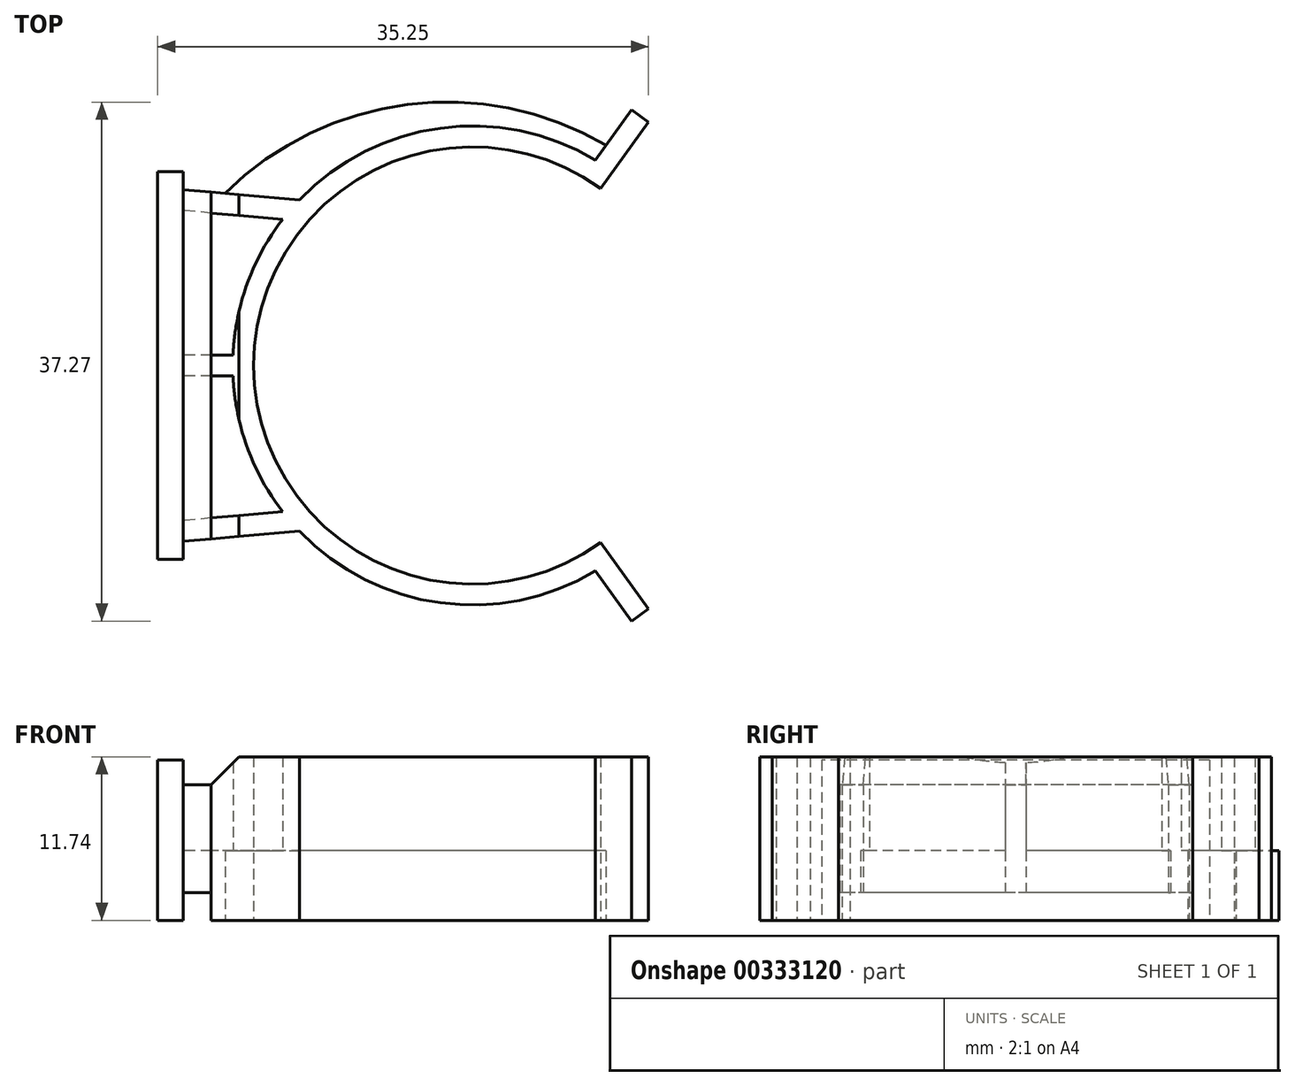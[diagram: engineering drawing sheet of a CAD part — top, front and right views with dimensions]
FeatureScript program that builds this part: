
annotation { "Feature Type Name" : "Feature", "Feature Type Description" : "" }
export const myFeature = defineFeature(function(context is Context, id is Id, definition is map)
    precondition{}
    {
        {
            var Q0;
            Q0=qCreatedBy(makeId("Top.planeOp"),FACE);
            var sketch = newSketch(context, id + "F0", { "sketchPlane" : qUnion([Q0])});
            skLineSegment(sketch, "E0.bottom", {"start": v(0, 13.91) * mm, "end": v(1.84, 13.91) * mm});
            skLineSegment(sketch, "E0.top", {"start": v(0, -13.91) * mm, "end": v(1.84, -13.91) * mm});
            skLineSegment(sketch, "E0.left", {"start": v(0, 13.91) * mm, "end": v(0, -13.91) * mm});
            skLineSegment(sketch, "E0.right", {"start": v(1.84, 13.91) * mm, "end": v(1.84, -13.91) * mm});
            skPoint(sketch, "E1", {"position": v(0, 0) * mm});
            skCircle(sketch, "E2", {"center": v(22.6, 0) * mm, "radius": 15.7 * mm});
            skLineSegment(sketch, "E3", {"start": v(31.8, 12.72) * mm, "end": v(31.8, -12.72) * mm, "construction": true});
            skLineSegment(sketch, "E4", {"start": v(1.84, 12.63) * mm, "end": v(1.84, -12.63) * mm, "construction": true});
            skLineSegment(sketch, "E5", {"start": v(4.84, 12.37) * mm, "end": v(4.84, -12.37) * mm, "construction": true});
            skPoint(sketch, "E6", {"position": v(1.84, 0) * mm});
            skPoint(sketch, "E7", {"position": v(4.84, 0) * mm});
            skLineSegment(sketch, "E8", {"start": v(9.39, 0) * mm, "end": v(48.03, 0) * mm, "construction": true});
            skPoint(sketch, "E8.endSnap0", {"position": v(31.8, 0) * mm});
            skCircle(sketch, "E9", {"center": v(22.6, 0) * mm, "radius": 17.2 * mm});
            skLineSegment(sketch, "E10", {"start": v(31.8, 12.72) * mm, "end": v(35.25, 17.48) * mm});
            skLineSegment(sketch, "E11", {"start": v(35.25, 17.48) * mm, "end": v(34.03, 18.36) * mm});
            skLineSegment(sketch, "E12", {"start": v(34.03, 18.36) * mm, "end": v(31.43, 14.76) * mm});
            skPoint(sketch, "E13", {"position": v(32.2, 15.83) * mm});
            skArc(sketch, "E14", {"start": v(32.2, 15.83) * mm, "mid": v(17.93, 18.74) * mm, "end": v(4.84, 12.37) * mm});
            skLineSegment(sketch, "E15", {"start": v(0, 13.91) * mm, "end": v(0, 18.91) * mm, "construction": true});
            skLineSegment(sketch, "E16", {"start": v(0, 18.91) * mm, "end": v(30.18, 18.91) * mm, "construction": true});
            skLineSegment(sketch, "E17", {"start": v(4.84, 12.37) * mm, "end": v(1.84, 12.63) * mm});
            skLineSegment(sketch, "E18", {"start": v(1.84, 12.63) * mm, "end": v(10.18, 11.9) * mm});
            skLineSegment(sketch, "E19", {"start": v(8.97, 10.5) * mm, "end": v(1.84, 11.13) * mm});
            skLineSegment(sketch, "E20", {"start": v(5.41, 0.75) * mm, "end": v(1.84, 0.75) * mm});
            skLineSegment(sketch, "E21.MirrorCS", {"start": v(4.84, -12.37) * mm, "end": v(1.84, -12.64) * mm});
            skArc(sketch, "E22.MirrorCS", {"start": v(32.2, -15.83) * mm, "mid": v(17.93, -18.74) * mm, "end": v(4.84, -12.37) * mm});
            skLineSegment(sketch, "E23.MirrorCS", {"start": v(34.03, -18.36) * mm, "end": v(31.43, -14.76) * mm});
            skLineSegment(sketch, "E24.MirrorCS", {"start": v(31.8, -12.72) * mm, "end": v(35.25, -17.48) * mm});
            skLineSegment(sketch, "E25.MirrorCS", {"start": v(35.25, -17.48) * mm, "end": v(34.03, -18.36) * mm});
            skLineSegment(sketch, "E26.MirrorCS", {"start": v(5.41, -0.75) * mm, "end": v(1.84, -0.75) * mm});
            skLineSegment(sketch, "E27.MirrorCS", {"start": v(1.84, -12.64) * mm, "end": v(10.18, -11.9) * mm});
            skLineSegment(sketch, "E28.MirrorCS", {"start": v(8.97, -10.5) * mm, "end": v(1.84, -11.13) * mm});
            skLineSegment(sketch, "E29", {"start": v(1.84, 12.63) * mm, "end": v(3.84, 12.63) * mm, "construction": true});
            skLineSegment(sketch, "E30", {"start": v(3.84, 12.46) * mm, "end": v(3.84, -12.5) * mm});
            skPoint(sketch, "E30.endSnap0", {"position": v(3.34, -12.5) * mm});
            skSolve(sketch);
        }
        {
            var Q0;
            {var subQ0=sQuery(id+"F0.wireOp",EDGE,"E20");var subQ1=sQuery(id+"F0.wireOp",EDGE,"E9");var subQ2=makeQuery(id+"F0.imprint","INTERSECT",VERTEX,{"derivedFrom":[subQ1,subQ0]});Q0=makeQuery(id+"F0.imprint","IMPRINT",FACE,{"disambiguationData":[TD([[makeQuery(id+"F0.imprint","IMPRINT",EDGE,{"disambiguationData":[TD([[subQ2,-1.0]])],"derivedFrom":subQ1}),-1.0]])]});}
            var Q1;
            {var subQ9=sQuery(id+"F0.wireOp",EDGE,"E2");var subQ11=sQuery(id+"F0.wireOp",EDGE,"E10");var subQ12=makeQuery(id+"F0.imprint","INTERSECT",VERTEX,{"derivedFrom":[subQ9,subQ11]});Q1=makeQuery(id+"F0.imprint","IMPRINT",FACE,{"disambiguationData":[TD([[makeQuery(id+"F0.imprint","IMPRINT",EDGE,{"disambiguationData":[TD([[subQ12,-1.0]])],"derivedFrom":subQ9}),-1.0]])]});}
            var Q2;
            {var subQ0=sQuery(id+"F0.wireOp",EDGE,"E25.MirrorCS");Q2=makeQuery(id+"F0.imprint","IMPRINT",FACE,{"disambiguationData":[TD([[makeQuery(id+"F0.imprint","IMPRINT",EDGE,{"derivedFrom":subQ0}),-1.0]])]});}
            var Q3;
            {var subQ1=sQuery(id+"F0.wireOp",EDGE,"E11");Q3=makeQuery(id+"F0.imprint","IMPRINT",FACE,{"disambiguationData":[TD([[makeQuery(id+"F0.imprint","IMPRINT",EDGE,{"derivedFrom":subQ1}),1.0]])]});}
            var Q4;
            {var subQ3=sQuery(id+"F0.wireOp",EDGE,"uS4j9IEw-3btY-5Asd-42hh-y3e24C7YOMrq");Q4=makeQuery(id+"F0.imprint","IMPRINT",FACE,{"disambiguationData":[TD([[makeQuery(id+"F0.imprint","IMPRINT",EDGE,{"derivedFrom":subQ3}),-1.0]])]});}
            var Q5;
            {var subQ3=sQuery(id+"F0.wireOp",EDGE,"GVzlFPN8-b27c-Kkxc-7IJt-Wx999ItFsk8j");Q5=makeQuery(id+"F0.imprint","IMPRINT",FACE,{"disambiguationData":[TD([[makeQuery(id+"F0.imprint","IMPRINT",EDGE,{"derivedFrom":subQ3}),-1.0]])]});}
            var Q6;
            {var subQ1=sQuery(id+"F0.wireOp",EDGE,"E9");var subQ5=sQuery(id+"F0.wireOp",EDGE,"E18");var subQ7=makeQuery(id+"F0.imprint","INTERSECT",VERTEX,{"derivedFrom":[subQ1,subQ5]});Q6=makeQuery(id+"F0.imprint","IMPRINT",FACE,{"disambiguationData":[TD([[makeQuery(id+"F0.imprint","IMPRINT",EDGE,{"disambiguationData":[TD([[subQ7,-1.0]])],"derivedFrom":subQ1}),-1.0]])]});}
            var Q7;
            {var subQ1=sQuery(id+"F0.wireOp",EDGE,"E9");var subQ5=sQuery(id+"F0.wireOp",EDGE,"E27.MirrorCS");var subQ7=makeQuery(id+"F0.imprint","INTERSECT",VERTEX,{"derivedFrom":[subQ1,subQ5]});Q7=makeQuery(id+"F0.imprint","IMPRINT",FACE,{"disambiguationData":[TD([[makeQuery(id+"F0.imprint","IMPRINT",EDGE,{"disambiguationData":[TD([[subQ7,1.0]])],"derivedFrom":subQ1}),-1.0]])]});}
            extrude(context, id + "F1", {"entities" : qUnion([Q0, Q1, Q2, Q3, Q4, Q5, Q6, Q7]), "depth" : 11.74 * mm});
        }
        {
            var Q0;
            {var subQ5=sQuery(id+"F0.wireOp",EDGE,"E14");Q0=makeQuery(id+"F0.imprint","IMPRINT",FACE,{"disambiguationData":[TD([[makeQuery(id+"F0.imprint","IMPRINT",EDGE,{"derivedFrom":subQ5}),1.0]])]});}
            var Q1;
            {var subQ0=sQuery(id+"F0.wireOp",EDGE,"6133e3dc-337a-4b65-9761-848ba6b2476f0.MirrorCS");Q1=makeQuery(id+"F0.imprint","IMPRINT",FACE,{"disambiguationData":[TD([[makeQuery(id+"F0.imprint","IMPRINT",EDGE,{"derivedFrom":subQ0}),-1.0]])]});}
            var Q2;
            {var subQ5=sQuery(id+"F0.wireOp",EDGE,"E22.MirrorCS");Q2=makeQuery(id+"F0.imprint","IMPRINT",FACE,{"disambiguationData":[TD([[makeQuery(id+"F0.imprint","IMPRINT",EDGE,{"derivedFrom":subQ5}),-1.0]])]});}
            var Q3;
            {var subQ0=sQuery(id+"F0.wireOp",EDGE,"E26.MirrorCS");var subQ1=sQuery(id+"F0.wireOp",EDGE,"E9");var subQ2=makeQuery(id+"F0.imprint","INTERSECT",VERTEX,{"derivedFrom":[subQ1,subQ0]});Q3=makeQuery(id+"F0.imprint","IMPRINT",FACE,{"disambiguationData":[TD([[makeQuery(id+"F0.imprint","IMPRINT",EDGE,{"disambiguationData":[TD([[subQ2,-1.0]])],"derivedFrom":subQ1}),-1.0]])]});}
            var Q4;
            {var subQ0=sQuery(id+"F0.wireOp",EDGE,"E19");var subQ1=sQuery(id+"F0.wireOp",EDGE,"E9");var subQ2=makeQuery(id+"F0.imprint","INTERSECT",VERTEX,{"derivedFrom":[subQ1,subQ0]});Q4=makeQuery(id+"F0.imprint","IMPRINT",FACE,{"disambiguationData":[TD([[makeQuery(id+"F0.imprint","IMPRINT",EDGE,{"disambiguationData":[TD([[subQ2,-1.0]])],"derivedFrom":subQ1}),-1.0]])]});}
            extrude(context, id + "F2", {"entities" : qUnion([Q0, Q1, Q2, Q3, Q4]), "operationType" : NewBodyOperationType.ADD, "depth" : 5 * mm});
        }
        {
            var Q0;
            {var subQ5=sQuery(id+"F0.wireOp",EDGE,"GVzlFPN8-b27c-Kkxc-7IJt-Wx999ItFsk8j");Q0=makeQuery(id+"F0.imprint","IMPRINT",FACE,{"disambiguationData":[TD([[makeQuery(id+"F0.imprint","IMPRINT",EDGE,{"derivedFrom":subQ5}),1.0]])]});}
            var Q1;
            {var subQ0=sQuery(id+"F0.wireOp",EDGE,"E20");var subQ1=sQuery(id+"F0.wireOp",EDGE,"E0.right");var subQ2=makeQuery(id+"F0.imprint","INTERSECT",VERTEX,{"derivedFrom":[subQ1,subQ0]});Q1=makeQuery(id+"F0.imprint","IMPRINT",FACE,{"disambiguationData":[TD([[makeQuery(id+"F0.imprint","IMPRINT",EDGE,{"disambiguationData":[TD([[subQ2,-1.0]])],"derivedFrom":subQ1}),1.0]])]});}
            var Q2;
            {var subQ5=sQuery(id+"F0.wireOp",EDGE,"uS4j9IEw-3btY-5Asd-42hh-y3e24C7YOMrq");Q2=makeQuery(id+"F0.imprint","IMPRINT",FACE,{"disambiguationData":[TD([[makeQuery(id+"F0.imprint","IMPRINT",EDGE,{"derivedFrom":subQ5}),1.0]])]});}
            var Q3;
            {var subQ0=sQuery(id+"F0.wireOp",EDGE,"E27.MirrorCS");var subQ1=sQuery(id+"F0.wireOp",EDGE,"E0.right");var subQ2=makeQuery(id+"F0.imprint","INTERSECT",VERTEX,{"derivedFrom":[subQ1,subQ0]});Q3=makeQuery(id+"F0.imprint","IMPRINT",FACE,{"disambiguationData":[TD([[makeQuery(id+"F0.imprint","IMPRINT",EDGE,{"disambiguationData":[TD([[subQ2,1.0]])],"derivedFrom":subQ1}),1.0]])]});}
            var Q4;
            {var subQ0=sQuery(id+"F0.wireOp",EDGE,"E18");var subQ1=sQuery(id+"F0.wireOp",EDGE,"E0.right");var subQ2=makeQuery(id+"F0.imprint","INTERSECT",VERTEX,{"derivedFrom":[subQ1,subQ0]});Q4=makeQuery(id+"F0.imprint","IMPRINT",FACE,{"disambiguationData":[TD([[makeQuery(id+"F0.imprint","IMPRINT",EDGE,{"disambiguationData":[TD([[subQ2,-1.0]])],"derivedFrom":subQ1}),1.0]])]});}
            extrude(context, id + "F3", {"entities" : qUnion([Q0, Q1, Q2, Q3, Q4]), "depth" : 9.74 * mm, "hasSecondDirection" : true, "secondDirectionOppositeDirection" : false, "secondDirectionDepth" : 2 * mm});
        }
        {
            var Q0;
            {var subQ0=sQuery(id+"F0.wireOp",EDGE,"E19");var subQ1=sQuery(id+"F0.wireOp",EDGE,"E0.right");var subQ2=makeQuery(id+"F0.imprint","INTERSECT",VERTEX,{"derivedFrom":[subQ1,subQ0]});Q0=makeQuery(id+"F0.imprint","IMPRINT",FACE,{"disambiguationData":[TD([[makeQuery(id+"F0.imprint","IMPRINT",EDGE,{"disambiguationData":[TD([[subQ2,-1.0]])],"derivedFrom":subQ1}),1.0]])]});}
            var Q1;
            {var subQ0=sQuery(id+"F0.wireOp",EDGE,"E26.MirrorCS");var subQ1=sQuery(id+"F0.wireOp",EDGE,"E0.right");var subQ2=makeQuery(id+"F0.imprint","INTERSECT",VERTEX,{"derivedFrom":[subQ1,subQ0]});Q1=makeQuery(id+"F0.imprint","IMPRINT",FACE,{"disambiguationData":[TD([[makeQuery(id+"F0.imprint","IMPRINT",EDGE,{"disambiguationData":[TD([[subQ2,-1.0]])],"derivedFrom":subQ1}),1.0]])]});}
            extrude(context, id + "F4", {"entities" : qUnion([Q0, Q1]), "depth" : 5 * mm, "hasSecondDirection" : true, "secondDirectionOppositeDirection" : false, "secondDirectionDepth" : 2 * mm});
        }
        {
            var Q0;
            {var subQ0=sQuery(id+"F0.wireOp",EDGE,"E30");Q0=makeQuery(id+"F1.opExtrude","CAP_EDGE",EDGE,{"disambiguationData":[OSD([subQ0]),TDD([makeQuery(id+"F0.imprint","IMPRINT",EDGE,{"disambiguationData":[TD([[makeQuery(id+"F0.imprint","INTERSECT",VERTEX,{"derivedFrom":[sQuery(id+"F0.wireOp",EDGE,"E20"),subQ0]}),-1.0]])],"derivedFrom":subQ0})])],"isStart":false});}
            var Q1;
            {var subQ0=sQuery(id+"F0.wireOp",EDGE,"E30");Q1=makeQuery(id+"F1.opExtrude","CAP_EDGE",EDGE,{"disambiguationData":[OSD([subQ0]),TDD([makeQuery(id+"F0.imprint","IMPRINT",EDGE,{"disambiguationData":[TD([[makeQuery(id+"F0.imprint","INTERSECT",VERTEX,{"derivedFrom":[sQuery(id+"F0.wireOp",EDGE,"E27.MirrorCS"),subQ0]}),1.0]])],"derivedFrom":subQ0})])],"isStart":false});}
            var Q2;
            {var subQ0=sQuery(id+"F0.wireOp",EDGE,"E30");Q2=makeQuery(id+"F1.opExtrude","CAP_EDGE",EDGE,{"disambiguationData":[OSD([subQ0]),TDD([makeQuery(id+"F0.imprint","IMPRINT",EDGE,{"disambiguationData":[TD([[makeQuery(id+"F0.imprint","INTERSECT",VERTEX,{"derivedFrom":[sQuery(id+"F0.wireOp",EDGE,"E18"),subQ0]}),-1.0]])],"derivedFrom":subQ0})])],"isStart":false});}
            chamfer(context, id + "F5", {"entities" : qUnion([Q0, Q1, Q2]), "width" : 2 * mm, "tangentPropagation" : true});
        }
        {
            var Q0;
            {var subQ1=sQuery(id+"F0.wireOp",EDGE,"E0.bottom");Q0=makeQuery(id+"F0.imprint","IMPRINT",FACE,{"disambiguationData":[TD([[makeQuery(id+"F0.imprint","IMPRINT",EDGE,{"derivedFrom":subQ1}),-1.0]])]});}
            extrude(context, id + "F6", {"entities" : qUnion([Q0]), "depth" : 11.5 * mm});
        }
    });
